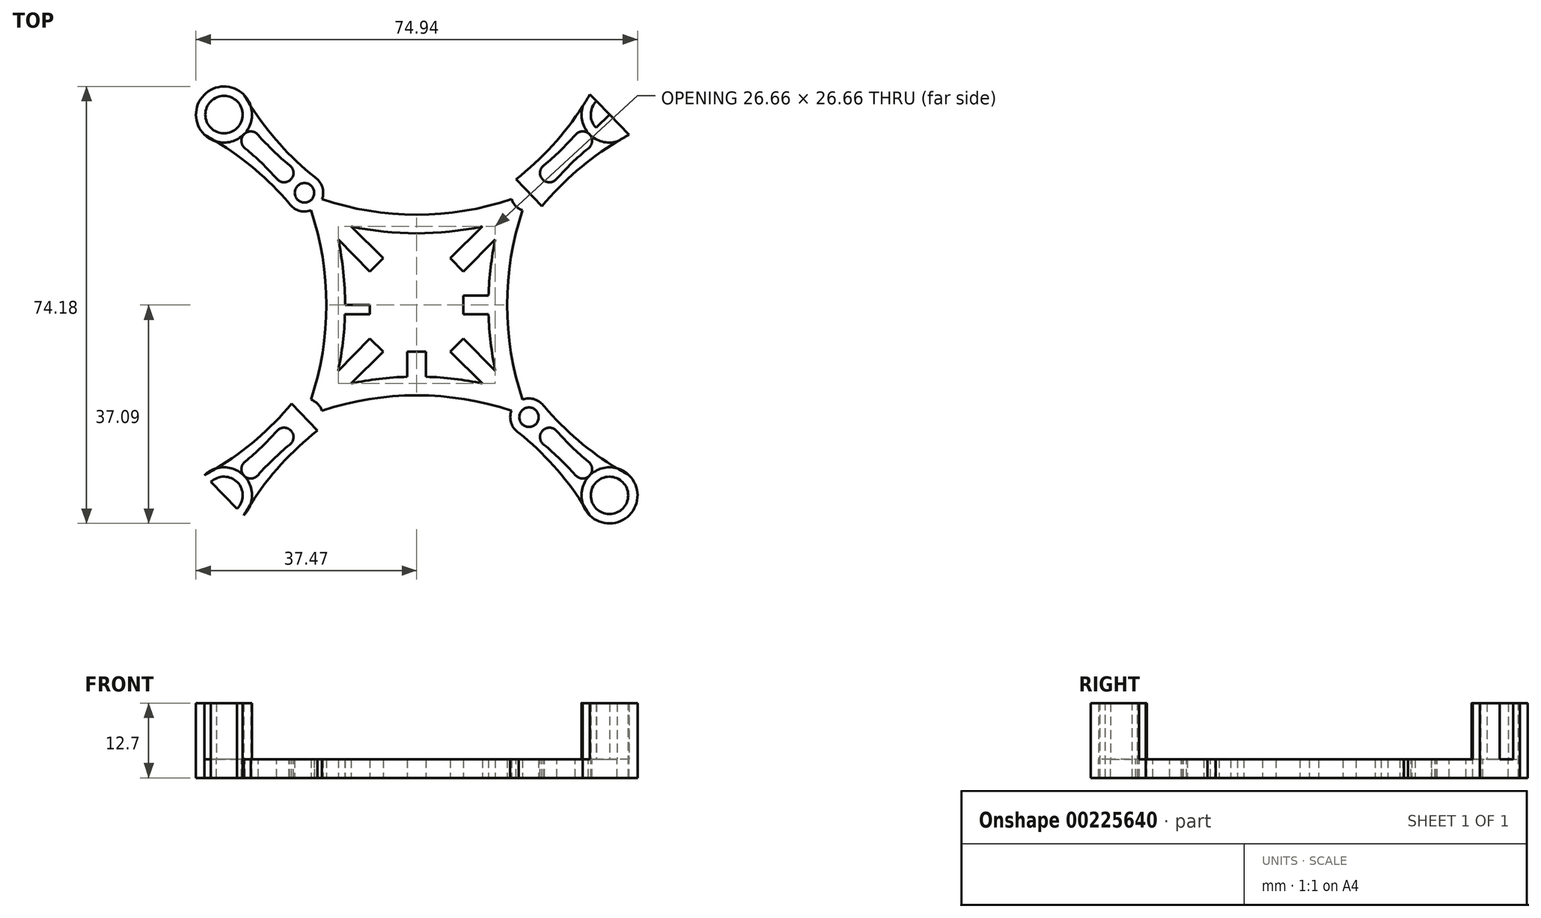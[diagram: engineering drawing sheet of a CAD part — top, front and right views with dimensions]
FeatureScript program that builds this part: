
annotation { "Feature Type Name" : "Feature", "Feature Type Description" : "" }
export const myFeature = defineFeature(function(context is Context, id is Id, definition is map)
    precondition{}
    {
        {
            var Q0;
            Q0=qCreatedBy(makeId("Top.planeOp"),FACE);
            var sketch = newSketch(context, id + "F0", { "sketchPlane" : qUnion([Q0])});
            skPoint(sketch, "E0.middle", {"position": v(0, 0) * mm});
            skLineSegment(sketch, "E1.bottom", {"start": v(-7.94, 7.94) * mm, "end": v(7.94, 7.94) * mm});
            skLineSegment(sketch, "E1.top", {"start": v(-7.94, -7.94) * mm, "end": v(7.94, -7.94) * mm});
            skLineSegment(sketch, "E1.left", {"start": v(-7.94, 7.94) * mm, "end": v(-7.94, -7.94) * mm});
            skLineSegment(sketch, "E1.right", {"start": v(7.94, 7.94) * mm, "end": v(7.94, -7.94) * mm});
            skCircle(sketch, "E2", {"center": v(-19.05, 19.05) * mm, "radius": 3.18 * mm});
            skCircle(sketch, "E3", {"center": v(-19.05, 19.05) * mm, "radius": 1.65 * mm});
            skCircle(sketch, "E4.MirrorC", {"center": v(19.05, 19.05) * mm, "radius": 3.18 * mm});
            skCircle(sketch, "E5.MirrorC", {"center": v(19.05, 19.05) * mm, "radius": 1.65 * mm});
            skCircle(sketch, "E6.MirrorC", {"center": v(-19.05, -19.05) * mm, "radius": 3.18 * mm});
            skCircle(sketch, "E7.MirrorC", {"center": v(-19.05, -19.05) * mm, "radius": 1.65 * mm});
            skCircle(sketch, "E8.MirrorC", {"center": v(19.05, -19.05) * mm, "radius": 3.18 * mm});
            skCircle(sketch, "E9.MirrorC", {"center": v(19.05, -19.05) * mm, "radius": 1.65 * mm});
            skArc(sketch, "E10", {"start": v(-19.05, 19.05) * mm, "mid": v(0, 15.34) * mm, "end": v(19.05, 19.05) * mm});
            skArc(sketch, "E11", {"start": v(19.05, 19.05) * mm, "mid": v(15.34, 0) * mm, "end": v(19.05, -19.05) * mm});
            skArc(sketch, "E12.MirrorCS", {"start": v(19.05, -19.05) * mm, "mid": v(15.34, 0) * mm, "end": v(19.05, 19.05) * mm});
            skArc(sketch, "E13.MirrorCS", {"start": v(19.05, 19.05) * mm, "mid": v(0, 15.34) * mm, "end": v(-19.05, 19.05) * mm});
            skArc(sketch, "E14.MirrorCS", {"start": v(-19.05, -19.05) * mm, "mid": v(-15.34, 0) * mm, "end": v(-19.05, 19.05) * mm});
            skArc(sketch, "E15.MirrorCS", {"start": v(19.05, -19.05) * mm, "mid": v(0, -15.34) * mm, "end": v(-19.05, -19.05) * mm});
            skArc(sketch, "E16.0", {"start": v(14.02, 14.02) * mm, "mid": v(0, 12.17) * mm, "end": v(-14.02, 14.02) * mm});
            skArc(sketch, "E16.1", {"start": v(14.02, 14.02) * mm, "mid": v(12.17, 0) * mm, "end": v(14.02, -14.02) * mm});
            skArc(sketch, "E16.2", {"start": v(14.02, -14.02) * mm, "mid": v(0, -12.17) * mm, "end": v(-14.02, -14.02) * mm});
            skArc(sketch, "E16.3", {"start": v(-14.02, -14.02) * mm, "mid": v(-12.17, 0) * mm, "end": v(-14.02, 14.02) * mm});
            skLineSegment(sketch, "E17.bottom", {"start": v(0, 7.94) * mm, "end": v(-1.59, 7.94) * mm});
            skLineSegment(sketch, "E17.top", {"start": v(0, 13.02) * mm, "end": v(-1.59, 13.02) * mm});
            skLineSegment(sketch, "E17.left", {"start": v(0, 7.94) * mm, "end": v(0, 13.02) * mm});
            skLineSegment(sketch, "E17.right", {"start": v(-1.59, 7.94) * mm, "end": v(-1.59, 13.02) * mm});
            skLineSegment(sketch, "E18.MirrorCS", {"start": v(-1.59, -7.94) * mm, "end": v(-1.59, -13.02) * mm});
            skLineSegment(sketch, "E19.MirrorCS", {"start": v(0, -7.94) * mm, "end": v(0, -13.02) * mm});
            skLineSegment(sketch, "E20.MirrorCS", {"start": v(0, -13.02) * mm, "end": v(-1.59, -13.02) * mm});
            skLineSegment(sketch, "E21.MirrorCS", {"start": v(0, -13.02) * mm, "end": v(1.59, -13.02) * mm});
            skLineSegment(sketch, "E22.MirrorCS", {"start": v(1.59, -7.94) * mm, "end": v(1.59, -13.02) * mm});
            skLineSegment(sketch, "E23.MirrorCS", {"start": v(7.94, -7.94) * mm, "end": v(-7.94, -7.94) * mm});
            skLineSegment(sketch, "E24.MirrorCS", {"start": v(1.59, 7.94) * mm, "end": v(1.59, 13.02) * mm});
            skLineSegment(sketch, "E25.MirrorCS", {"start": v(0, 13.02) * mm, "end": v(1.59, 13.02) * mm});
            skLineSegment(sketch, "E26.bottom", {"start": v(-7.94, 0) * mm, "end": v(-13.02, 0) * mm});
            skLineSegment(sketch, "E26.top", {"start": v(-7.94, 1.59) * mm, "end": v(-13.02, 1.59) * mm});
            skLineSegment(sketch, "E26.left", {"start": v(-7.94, 0) * mm, "end": v(-7.94, 1.59) * mm});
            skLineSegment(sketch, "E26.right", {"start": v(-13.02, 0) * mm, "end": v(-13.02, 1.59) * mm});
            skLineSegment(sketch, "E27.MirrorCS", {"start": v(7.94, 1.59) * mm, "end": v(13.02, 1.59) * mm});
            skLineSegment(sketch, "E28.MirrorCS", {"start": v(13.02, 0) * mm, "end": v(13.02, 1.59) * mm});
            skLineSegment(sketch, "E29.MirrorCS", {"start": v(7.94, 0) * mm, "end": v(13.02, 0) * mm});
            skLineSegment(sketch, "E30.MirrorCS", {"start": v(-13.02, 0) * mm, "end": v(-13.02, -1.59) * mm});
            skLineSegment(sketch, "E31.MirrorCS", {"start": v(-7.94, -1.59) * mm, "end": v(-13.02, -1.59) * mm});
            skLineSegment(sketch, "E32.MirrorCS", {"start": v(7.94, -1.59) * mm, "end": v(13.02, -1.59) * mm});
            skLineSegment(sketch, "E33.MirrorCS", {"start": v(13.02, 0) * mm, "end": v(13.02, -1.59) * mm});
            skLineSegment(sketch, "E34", {"start": v(-7.94, 5.7) * mm, "end": v(-5.7, 7.94) * mm});
            skLineSegment(sketch, "E35", {"start": v(-7.94, 7.94) * mm, "end": v(-6.81, 6.81) * mm});
            skLineSegment(sketch, "E36", {"start": v(-7.94, 5.7) * mm, "end": v(-13.33, 11.15) * mm});
            skLineSegment(sketch, "E37", {"start": v(-13.33, 11.15) * mm, "end": v(-11.13, 13.33) * mm});
            skLineSegment(sketch, "E38", {"start": v(-11.13, 13.33) * mm, "end": v(-5.7, 7.94) * mm});
            skLineSegment(sketch, "E39.MirrorCS", {"start": v(11.13, 13.33) * mm, "end": v(5.7, 7.94) * mm});
            skLineSegment(sketch, "E40.MirrorCS", {"start": v(7.94, 5.7) * mm, "end": v(5.7, 7.94) * mm});
            skLineSegment(sketch, "E41.MirrorCS", {"start": v(7.94, 5.7) * mm, "end": v(13.33, 11.15) * mm});
            skLineSegment(sketch, "E42.MirrorCS", {"start": v(13.33, 11.15) * mm, "end": v(11.13, 13.33) * mm});
            skLineSegment(sketch, "E43.MirrorCS", {"start": v(7.94, -5.7) * mm, "end": v(13.33, -11.15) * mm});
            skLineSegment(sketch, "E44.MirrorCS", {"start": v(7.94, -5.7) * mm, "end": v(5.7, -7.94) * mm});
            skLineSegment(sketch, "E45.MirrorCS", {"start": v(11.13, -13.33) * mm, "end": v(5.7, -7.94) * mm});
            skLineSegment(sketch, "E46.MirrorCS", {"start": v(-7.94, -5.7) * mm, "end": v(-5.7, -7.94) * mm});
            skLineSegment(sketch, "E47.MirrorCS", {"start": v(-11.13, -13.33) * mm, "end": v(-5.7, -7.94) * mm});
            skLineSegment(sketch, "E48.MirrorCS", {"start": v(-13.33, -11.15) * mm, "end": v(-11.13, -13.33) * mm});
            skLineSegment(sketch, "E49.MirrorCS", {"start": v(-7.94, -5.7) * mm, "end": v(-13.33, -11.15) * mm});
            skLineSegment(sketch, "E50.MirrorCS", {"start": v(13.33, -11.15) * mm, "end": v(11.13, -13.33) * mm});
            skLineSegment(sketch, "E51", {"start": v(19.05, -19.05) * mm, "end": v(16.8, -16.81) * mm});
            skPoint(sketch, "E52", {"position": v(17.08, -17.1) * mm});
            skLineSegment(sketch, "E53", {"start": v(17.08, -17.1) * mm, "end": v(17.64, -16.53) * mm});
            skLineSegment(sketch, "E54", {"start": v(17.64, -16.53) * mm, "end": v(16.5, -15.41) * mm});
            skLineSegment(sketch, "E55", {"start": v(16.5, -15.41) * mm, "end": v(15.95, -15.98) * mm});
            skLineSegment(sketch, "E56", {"start": v(15.95, -15.98) * mm, "end": v(16.8, -16.81) * mm});
            skLineSegment(sketch, "E57.MirrorCS", {"start": v(15.4, -16.54) * mm, "end": v(15.95, -15.98) * mm});
            skLineSegment(sketch, "E58.MirrorCS", {"start": v(16.52, -17.66) * mm, "end": v(15.4, -16.54) * mm});
            skLineSegment(sketch, "E59.MirrorCS", {"start": v(17.08, -17.1) * mm, "end": v(16.52, -17.66) * mm});
            skLineSegment(sketch, "E60", {"start": v(15.4, -16.54) * mm, "end": v(14.26, -15.42) * mm});
            skLineSegment(sketch, "E61", {"start": v(14.26, -15.42) * mm, "end": v(15.38, -14.3) * mm});
            skLineSegment(sketch, "E62", {"start": v(15.38, -14.3) * mm, "end": v(16.5, -15.41) * mm});
            skLineSegment(sketch, "E63", {"start": v(15.1, -16.26) * mm, "end": v(16.23, -15.13) * mm});
            skLineSegment(sketch, "E64.MirrorCS", {"start": v(-15.4, -16.54) * mm, "end": v(-14.26, -15.42) * mm});
            skLineSegment(sketch, "E65.MirrorCS", {"start": v(-15.1, -16.26) * mm, "end": v(-16.23, -15.13) * mm});
            skLineSegment(sketch, "E66.MirrorCS", {"start": v(-15.38, -14.3) * mm, "end": v(-16.5, -15.41) * mm});
            skLineSegment(sketch, "E67.MirrorCS", {"start": v(-14.26, -15.42) * mm, "end": v(-15.38, -14.3) * mm});
            skLineSegment(sketch, "E68.MirrorCS", {"start": v(15.38, 14.3) * mm, "end": v(16.5, 15.41) * mm});
            skLineSegment(sketch, "E69.MirrorCS", {"start": v(15.1, 16.26) * mm, "end": v(16.23, 15.13) * mm});
            skLineSegment(sketch, "E70.MirrorCS", {"start": v(15.4, 16.54) * mm, "end": v(14.26, 15.42) * mm});
            skLineSegment(sketch, "E71.MirrorCS", {"start": v(14.26, 15.42) * mm, "end": v(15.38, 14.3) * mm});
            skLineSegment(sketch, "E72.MirrorCS", {"start": v(-15.38, 14.3) * mm, "end": v(-16.5, 15.41) * mm});
            skLineSegment(sketch, "E73.MirrorCS", {"start": v(-15.4, 16.54) * mm, "end": v(-14.26, 15.42) * mm});
            skLineSegment(sketch, "E74.MirrorCS", {"start": v(-14.26, 15.42) * mm, "end": v(-15.38, 14.3) * mm});
            skLineSegment(sketch, "E75.MirrorCS", {"start": v(-15.1, 16.26) * mm, "end": v(-16.23, 15.13) * mm});
            skSolve(sketch);
        }
        {
            var Q0;
            {var subQ0=sQuery(id+"F0.wireOp",EDGE,"E13.MirrorCS");var subQ1=sQuery(id+"F0.wireOp",EDGE,"E2");var subQ2=makeQuery(id+"F0.imprint","INTERSECT",VERTEX,{"derivedFrom":[subQ1,subQ0]});Q0=makeQuery(id+"F0.imprint","IMPRINT",FACE,{"disambiguationData":[TD([[makeQuery(id+"F0.imprint","IMPRINT",EDGE,{"disambiguationData":[TD([[subQ2,-1.0]])],"derivedFrom":subQ1}),1.0]])]});}
            var Q1;
            {var subQ0=sQuery(id+"F0.wireOp",EDGE,"E13.MirrorCS");var subQ1=sQuery(id+"F0.wireOp",EDGE,"E2");var subQ2=makeQuery(id+"F0.imprint","INTERSECT",VERTEX,{"derivedFrom":[subQ1,subQ0]});Q1=makeQuery(id+"F0.imprint","IMPRINT",FACE,{"disambiguationData":[TD([[makeQuery(id+"F0.imprint","IMPRINT",EDGE,{"disambiguationData":[TD([[subQ2,1.0]])],"derivedFrom":subQ1}),1.0]])]});}
            var Q2;
            {var subQ26=sQuery(id+"F0.wireOp",EDGE,"E17.top");Q2=makeQuery(id+"F0.imprint","IMPRINT",FACE,{"disambiguationData":[TD([[makeQuery(id+"F0.imprint","IMPRINT",EDGE,{"derivedFrom":subQ26}),-1.0]])]});}
            var Q3;
            {var subQ0=sQuery(id+"F0.wireOp",EDGE,"E11");var subQ1=sQuery(id+"F0.wireOp",EDGE,"E4.MirrorC");var subQ2=makeQuery(id+"F0.imprint","INTERSECT",VERTEX,{"derivedFrom":[subQ1,subQ0]});Q3=makeQuery(id+"F0.imprint","IMPRINT",FACE,{"disambiguationData":[TD([[makeQuery(id+"F0.imprint","IMPRINT",EDGE,{"disambiguationData":[TD([[subQ2,-1.0]])],"derivedFrom":subQ1}),-1.0]])]});}
            var Q4;
            {var subQ0=sQuery(id+"F0.wireOp",EDGE,"E11");var subQ1=sQuery(id+"F0.wireOp",EDGE,"E4.MirrorC");var subQ2=makeQuery(id+"F0.imprint","INTERSECT",VERTEX,{"derivedFrom":[subQ1,subQ0]});Q4=makeQuery(id+"F0.imprint","IMPRINT",FACE,{"disambiguationData":[TD([[makeQuery(id+"F0.imprint","IMPRINT",EDGE,{"disambiguationData":[TD([[subQ2,1.0]])],"derivedFrom":subQ1}),-1.0]])]});}
            var Q5;
            {var subQ5=sQuery(id+"F0.wireOp",EDGE,"E17.top");Q5=makeQuery(id+"F0.imprint","IMPRINT",FACE,{"disambiguationData":[TD([[makeQuery(id+"F0.imprint","IMPRINT",EDGE,{"derivedFrom":subQ5}),1.0]])]});}
            var Q6;
            {var subQ3=sQuery(id+"F0.wireOp",EDGE,"E37");Q6=makeQuery(id+"F0.imprint","IMPRINT",FACE,{"disambiguationData":[TD([[makeQuery(id+"F0.imprint","IMPRINT",EDGE,{"derivedFrom":subQ3}),1.0]])]});}
            var Q7;
            {var subQ5=sQuery(id+"F0.wireOp",EDGE,"E25.MirrorCS");Q7=makeQuery(id+"F0.imprint","IMPRINT",FACE,{"disambiguationData":[TD([[makeQuery(id+"F0.imprint","IMPRINT",EDGE,{"derivedFrom":subQ5}),-1.0]])]});}
            var Q8;
            {var subQ3=sQuery(id+"F0.wireOp",EDGE,"E42.MirrorCS");Q8=makeQuery(id+"F0.imprint","IMPRINT",FACE,{"disambiguationData":[TD([[makeQuery(id+"F0.imprint","IMPRINT",EDGE,{"derivedFrom":subQ3}),-1.0]])]});}
            var Q9;
            {var subQ1=sQuery(id+"F0.wireOp",EDGE,"E39.MirrorCS");Q9=makeQuery(id+"F0.imprint","IMPRINT",FACE,{"disambiguationData":[TD([[makeQuery(id+"F0.imprint","IMPRINT",EDGE,{"derivedFrom":subQ1}),1.0]])]});}
            var Q10;
            {var subQ5=sQuery(id+"F0.wireOp",EDGE,"E36");Q10=makeQuery(id+"F0.imprint","IMPRINT",FACE,{"disambiguationData":[TD([[makeQuery(id+"F0.imprint","IMPRINT",EDGE,{"derivedFrom":subQ5}),-1.0]])]});}
            var Q11;
            {var subQ5=sQuery(id+"F0.wireOp",EDGE,"E17.bottom");Q11=makeQuery(id+"F0.imprint","IMPRINT",FACE,{"disambiguationData":[TD([[makeQuery(id+"F0.imprint","IMPRINT",EDGE,{"derivedFrom":subQ5}),-1.0]])]});}
            var Q12;
            {var subQ3=sQuery(id+"F0.wireOp",EDGE,"E24.MirrorCS");var subQ5=sQuery(id+"F0.wireOp",EDGE,"E16.0");var subQ6=makeQuery(id+"F0.imprint","INTERSECT",VERTEX,{"derivedFrom":[subQ5,subQ3]});Q12=makeQuery(id+"F0.imprint","IMPRINT",FACE,{"disambiguationData":[TD([[makeQuery(id+"F0.imprint","IMPRINT",EDGE,{"disambiguationData":[TD([[subQ6,-1.0]])],"derivedFrom":subQ5}),1.0]])]});}
            var Q13;
            {var subQ0=sQuery(id+"F0.wireOp",EDGE,"E35");Q13=makeQuery(id+"F0.imprint","IMPRINT",FACE,{"disambiguationData":[TD([[makeQuery(id+"F0.imprint","IMPRINT",EDGE,{"derivedFrom":subQ0}),1.0]])]});}
            var Q14;
            {var subQ0=sQuery(id+"F0.wireOp",EDGE,"E35");Q14=makeQuery(id+"F0.imprint","IMPRINT",FACE,{"disambiguationData":[TD([[makeQuery(id+"F0.imprint","IMPRINT",EDGE,{"derivedFrom":subQ0}),-1.0]])]});}
            var Q15;
            {var subQ3=sQuery(id+"F0.wireOp",EDGE,"E40.MirrorCS");Q15=makeQuery(id+"F0.imprint","IMPRINT",FACE,{"disambiguationData":[TD([[makeQuery(id+"F0.imprint","IMPRINT",EDGE,{"derivedFrom":subQ3}),-1.0]])]});}
            var Q16;
            {var subQ12=sQuery(id+"F0.wireOp",EDGE,"E17.bottom");Q16=makeQuery(id+"F0.imprint","IMPRINT",FACE,{"disambiguationData":[TD([[makeQuery(id+"F0.imprint","IMPRINT",EDGE,{"derivedFrom":subQ12}),1.0]])]});}
            var Q17;
            {var subQ5=sQuery(id+"F0.wireOp",EDGE,"E26.right");Q17=makeQuery(id+"F0.imprint","IMPRINT",FACE,{"disambiguationData":[TD([[makeQuery(id+"F0.imprint","IMPRINT",EDGE,{"derivedFrom":subQ5}),-1.0]])]});}
            var Q18;
            {var subQ5=sQuery(id+"F0.wireOp",EDGE,"E30.MirrorCS");Q18=makeQuery(id+"F0.imprint","IMPRINT",FACE,{"disambiguationData":[TD([[makeQuery(id+"F0.imprint","IMPRINT",EDGE,{"derivedFrom":subQ5}),1.0]])]});}
            var Q19;
            {var subQ3=sQuery(id+"F0.wireOp",EDGE,"E31.MirrorCS");var subQ5=sQuery(id+"F0.wireOp",EDGE,"E16.3");var subQ6=makeQuery(id+"F0.imprint","INTERSECT",VERTEX,{"derivedFrom":[subQ5,subQ3]});Q19=makeQuery(id+"F0.imprint","IMPRINT",FACE,{"disambiguationData":[TD([[makeQuery(id+"F0.imprint","IMPRINT",EDGE,{"disambiguationData":[TD([[subQ6,-1.0]])],"derivedFrom":subQ5}),-1.0]])]});}
            var Q20;
            {var subQ5=sQuery(id+"F0.wireOp",EDGE,"E26.left");Q20=makeQuery(id+"F0.imprint","IMPRINT",FACE,{"disambiguationData":[TD([[makeQuery(id+"F0.imprint","IMPRINT",EDGE,{"derivedFrom":subQ5}),1.0]])]});}
            var Q21;
            {var subQ5=sQuery(id+"F0.wireOp",EDGE,"E28.MirrorCS");Q21=makeQuery(id+"F0.imprint","IMPRINT",FACE,{"disambiguationData":[TD([[makeQuery(id+"F0.imprint","IMPRINT",EDGE,{"derivedFrom":subQ5}),1.0]])]});}
            var Q22;
            {var subQ5=sQuery(id+"F0.wireOp",EDGE,"E33.MirrorCS");Q22=makeQuery(id+"F0.imprint","IMPRINT",FACE,{"disambiguationData":[TD([[makeQuery(id+"F0.imprint","IMPRINT",EDGE,{"derivedFrom":subQ5}),-1.0]])]});}
            var Q23;
            {var subQ3=sQuery(id+"F0.wireOp",EDGE,"E46.MirrorCS");Q23=makeQuery(id+"F0.imprint","IMPRINT",FACE,{"disambiguationData":[TD([[makeQuery(id+"F0.imprint","IMPRINT",EDGE,{"derivedFrom":subQ3}),-1.0]])]});}
            var Q24;
            {var subQ3=sQuery(id+"F0.wireOp",EDGE,"E48.MirrorCS");Q24=makeQuery(id+"F0.imprint","IMPRINT",FACE,{"disambiguationData":[TD([[makeQuery(id+"F0.imprint","IMPRINT",EDGE,{"derivedFrom":subQ3}),-1.0]])]});}
            var Q25;
            {var subQ0=sQuery(id+"F0.wireOp",EDGE,"E14.MirrorCS");var subQ1=sQuery(id+"F0.wireOp",EDGE,"E6.MirrorC");var subQ2=makeQuery(id+"F0.imprint","INTERSECT",VERTEX,{"derivedFrom":[subQ1,subQ0]});Q25=makeQuery(id+"F0.imprint","IMPRINT",FACE,{"disambiguationData":[TD([[makeQuery(id+"F0.imprint","IMPRINT",EDGE,{"disambiguationData":[TD([[subQ2,-1.0]])],"derivedFrom":subQ1}),-1.0]])]});}
            var Q26;
            {var subQ0=sQuery(id+"F0.wireOp",EDGE,"E14.MirrorCS");var subQ1=sQuery(id+"F0.wireOp",EDGE,"E6.MirrorC");var subQ2=makeQuery(id+"F0.imprint","INTERSECT",VERTEX,{"derivedFrom":[subQ1,subQ0]});Q26=makeQuery(id+"F0.imprint","IMPRINT",FACE,{"disambiguationData":[TD([[makeQuery(id+"F0.imprint","IMPRINT",EDGE,{"disambiguationData":[TD([[subQ2,1.0]])],"derivedFrom":subQ1}),-1.0]])]});}
            var Q27;
            {var subQ5=sQuery(id+"F0.wireOp",EDGE,"E20.MirrorCS");Q27=makeQuery(id+"F0.imprint","IMPRINT",FACE,{"disambiguationData":[TD([[makeQuery(id+"F0.imprint","IMPRINT",EDGE,{"derivedFrom":subQ5}),-1.0]])]});}
            var Q28;
            {var subQ5=sQuery(id+"F0.wireOp",EDGE,"E21.MirrorCS");Q28=makeQuery(id+"F0.imprint","IMPRINT",FACE,{"disambiguationData":[TD([[makeQuery(id+"F0.imprint","IMPRINT",EDGE,{"derivedFrom":subQ5}),1.0]])]});}
            var Q29;
            {var subQ0=sQuery(id+"F0.wireOp",EDGE,"E11");var subQ1=sQuery(id+"F0.wireOp",EDGE,"E8.MirrorC");var subQ2=makeQuery(id+"F0.imprint","INTERSECT",VERTEX,{"derivedFrom":[subQ1,subQ0]});Q29=makeQuery(id+"F0.imprint","IMPRINT",FACE,{"disambiguationData":[TD([[makeQuery(id+"F0.imprint","IMPRINT",EDGE,{"disambiguationData":[TD([[subQ2,1.0]])],"derivedFrom":subQ1}),1.0]])]});}
            var Q30;
            {var subQ0=sQuery(id+"F0.wireOp",EDGE,"E11");var subQ1=sQuery(id+"F0.wireOp",EDGE,"E8.MirrorC");var subQ2=makeQuery(id+"F0.imprint","INTERSECT",VERTEX,{"derivedFrom":[subQ1,subQ0]});Q30=makeQuery(id+"F0.imprint","IMPRINT",FACE,{"disambiguationData":[TD([[makeQuery(id+"F0.imprint","IMPRINT",EDGE,{"disambiguationData":[TD([[subQ2,-1.0]])],"derivedFrom":subQ1}),1.0]])]});}
            var Q31;
            {var subQ0=sQuery(id+"F0.wireOp",EDGE,"E29.MirrorCS");var subQ1=sQuery(id+"F0.wireOp",EDGE,"E1.right");var subQ2=makeQuery(id+"F0.imprint","INTERSECT",VERTEX,{"derivedFrom":[subQ1,subQ0]});Q31=makeQuery(id+"F0.imprint","IMPRINT",FACE,{"disambiguationData":[TD([[makeQuery(id+"F0.imprint","IMPRINT",EDGE,{"disambiguationData":[TD([[subQ2,-1.0]])],"derivedFrom":subQ1}),1.0]])]});}
            var Q32;
            {var subQ0=sQuery(id+"F0.wireOp",EDGE,"E27.MirrorCS");var subQ1=sQuery(id+"F0.wireOp",EDGE,"E1.right");var subQ2=makeQuery(id+"F0.imprint","INTERSECT",VERTEX,{"derivedFrom":[subQ1,subQ0]});Q32=makeQuery(id+"F0.imprint","IMPRINT",FACE,{"disambiguationData":[TD([[makeQuery(id+"F0.imprint","IMPRINT",EDGE,{"disambiguationData":[TD([[subQ2,-1.0]])],"derivedFrom":subQ1}),1.0]])]});}
            var Q33;
            {var subQ0=sQuery(id+"F0.wireOp",EDGE,"E47.MirrorCS");Q33=makeQuery(id+"F0.imprint","IMPRINT",FACE,{"disambiguationData":[TD([[makeQuery(id+"F0.imprint","IMPRINT",EDGE,{"derivedFrom":subQ0}),1.0]])]});}
            var Q34;
            {var subQ3=sQuery(id+"F0.wireOp",EDGE,"E44.MirrorCS");Q34=makeQuery(id+"F0.imprint","IMPRINT",FACE,{"disambiguationData":[TD([[makeQuery(id+"F0.imprint","IMPRINT",EDGE,{"derivedFrom":subQ3}),1.0]])]});}
            var Q35;
            {var subQ3=sQuery(id+"F0.wireOp",EDGE,"E50.MirrorCS");Q35=makeQuery(id+"F0.imprint","IMPRINT",FACE,{"disambiguationData":[TD([[makeQuery(id+"F0.imprint","IMPRINT",EDGE,{"derivedFrom":subQ3}),1.0]])]});}
            var Q36;
            {var subQ1=sQuery(id+"F0.wireOp",EDGE,"E43.MirrorCS");Q36=makeQuery(id+"F0.imprint","IMPRINT",FACE,{"disambiguationData":[TD([[makeQuery(id+"F0.imprint","IMPRINT",EDGE,{"derivedFrom":subQ1}),-1.0]])]});}
            var Q37;
            {var subQ0=sQuery(id+"F0.wireOp",EDGE,"E22.MirrorCS");var subQ1=sQuery(id+"F0.wireOp",EDGE,"E16.2");var subQ2=makeQuery(id+"F0.imprint","INTERSECT",VERTEX,{"derivedFrom":[subQ1,subQ0]});Q37=makeQuery(id+"F0.imprint","IMPRINT",FACE,{"disambiguationData":[TD([[makeQuery(id+"F0.imprint","IMPRINT",EDGE,{"disambiguationData":[TD([[subQ2,-1.0]])],"derivedFrom":subQ1}),-1.0]])]});}
            var Q38;
            {var subQ0=sQuery(id+"F0.wireOp",EDGE,"E19.MirrorCS");var subQ1=sQuery(id+"F0.wireOp",EDGE,"E16.2");var subQ2=makeQuery(id+"F0.imprint","INTERSECT",VERTEX,{"derivedFrom":[subQ1,subQ0]});Q38=makeQuery(id+"F0.imprint","IMPRINT",FACE,{"disambiguationData":[TD([[makeQuery(id+"F0.imprint","IMPRINT",EDGE,{"disambiguationData":[TD([[subQ2,-1.0]])],"derivedFrom":subQ1}),-1.0]])]});}
            var Q39;
            {var subQ5=sQuery(id+"F0.wireOp",EDGE,"E59.MirrorCS");Q39=makeQuery(id+"F0.imprint","IMPRINT",FACE,{"disambiguationData":[TD([[makeQuery(id+"F0.imprint","IMPRINT",EDGE,{"derivedFrom":subQ5}),1.0]])]});}
            var Q40;
            {var subQ0=sQuery(id+"F0.wireOp",EDGE,"E56");Q40=makeQuery(id+"F0.imprint","IMPRINT",FACE,{"disambiguationData":[TD([[makeQuery(id+"F0.imprint","IMPRINT",EDGE,{"derivedFrom":subQ0}),-1.0]])]});}
            var Q41;
            {var subQ5=sQuery(id+"F0.wireOp",EDGE,"E59.MirrorCS");Q41=makeQuery(id+"F0.imprint","IMPRINT",FACE,{"disambiguationData":[TD([[makeQuery(id+"F0.imprint","IMPRINT",EDGE,{"derivedFrom":subQ5}),-1.0]])]});}
            var Q42;
            {var subQ5=sQuery(id+"F0.wireOp",EDGE,"E53");Q42=makeQuery(id+"F0.imprint","IMPRINT",FACE,{"disambiguationData":[TD([[makeQuery(id+"F0.imprint","IMPRINT",EDGE,{"derivedFrom":subQ5}),1.0]])]});}
            var Q43;
            {var subQ4=sQuery(id+"F0.wireOp",EDGE,"E55");Q43=makeQuery(id+"F0.imprint","IMPRINT",FACE,{"disambiguationData":[TD([[makeQuery(id+"F0.imprint","IMPRINT",EDGE,{"derivedFrom":subQ4}),1.0]])]});}
            var Q44;
            {var subQ1=sQuery(id+"F0.wireOp",EDGE,"E55");Q44=makeQuery(id+"F0.imprint","IMPRINT",FACE,{"disambiguationData":[TD([[makeQuery(id+"F0.imprint","IMPRINT",EDGE,{"derivedFrom":subQ1}),-1.0]])]});}
            var Q45;
            {var subQ2=sQuery(id+"F0.wireOp",EDGE,"E69.MirrorCS");Q45=makeQuery(id+"F0.imprint","IMPRINT",FACE,{"disambiguationData":[TD([[makeQuery(id+"F0.imprint","IMPRINT",EDGE,{"derivedFrom":subQ2}),-1.0]])]});}
            var Q46;
            {var subQ0=sQuery(id+"F0.wireOp",EDGE,"E61");Q46=makeQuery(id+"F0.imprint","IMPRINT",FACE,{"disambiguationData":[TD([[makeQuery(id+"F0.imprint","IMPRINT",EDGE,{"derivedFrom":subQ0}),-1.0]])]});}
            var Q47;
            {var subQ2=sQuery(id+"F0.wireOp",EDGE,"E65.MirrorCS");Q47=makeQuery(id+"F0.imprint","IMPRINT",FACE,{"disambiguationData":[TD([[makeQuery(id+"F0.imprint","IMPRINT",EDGE,{"derivedFrom":subQ2}),-1.0]])]});}
            var Q48;
            {var subQ0=sQuery(id+"F0.wireOp",EDGE,"E74.MirrorCS");Q48=makeQuery(id+"F0.imprint","IMPRINT",FACE,{"disambiguationData":[TD([[makeQuery(id+"F0.imprint","IMPRINT",EDGE,{"derivedFrom":subQ0}),-1.0]])]});}
            extrude(context, id + "F1", {"entities" : qUnion([Q0, Q1, Q2, Q3, Q4, Q5, Q6, Q7, Q8, Q9, Q10, Q11, Q12, Q13, Q14, Q15, Q16, Q17, Q18, Q19, Q20, Q21, Q22, Q23, Q24, Q25, Q26, Q27, Q28, Q29, Q30, Q31, Q32, Q33, Q34, Q35, Q36, Q37, Q38, Q39, Q40, Q41, Q42, Q43, Q44, Q45, Q46, Q47, Q48]), "depth" : 3.17 * mm});
        }
        {
            var Q0;
            Q0=makeQuery(id+"F1.opExtrude","CAP_FACE",FACE,{"disambiguationData":[OSD([sQuery(id+"F0.wireOp",EDGE,"E1.bottom"),sQuery(id+"F0.wireOp",EDGE,"E1.left"),sQuery(id+"F0.wireOp",EDGE,"E1.right"),sQuery(id+"F0.wireOp",EDGE,"E2"),sQuery(id+"F0.wireOp",EDGE,"E3"),sQuery(id+"F0.wireOp",EDGE,"E4.MirrorC"),sQuery(id+"F0.wireOp",EDGE,"E5.MirrorC"),sQuery(id+"F0.wireOp",EDGE,"E6.MirrorC"),sQuery(id+"F0.wireOp",EDGE,"E7.MirrorC"),sQuery(id+"F0.wireOp",EDGE,"E8.MirrorC"),sQuery(id+"F0.wireOp",EDGE,"E9.MirrorC"),sQuery(id+"F0.wireOp",EDGE,"E11"),sQuery(id+"F0.wireOp",EDGE,"E13.MirrorCS"),sQuery(id+"F0.wireOp",EDGE,"E14.MirrorCS"),sQuery(id+"F0.wireOp",EDGE,"E15.MirrorCS"),sQuery(id+"F0.wireOp",EDGE,"E16.0"),sQuery(id+"F0.wireOp",EDGE,"E16.1"),sQuery(id+"F0.wireOp",EDGE,"E16.2"),sQuery(id+"F0.wireOp",EDGE,"E16.3"),sQuery(id+"F0.wireOp",EDGE,"E17.right"),sQuery(id+"F0.wireOp",EDGE,"E18.MirrorCS"),sQuery(id+"F0.wireOp",EDGE,"E22.MirrorCS"),sQuery(id+"F0.wireOp",EDGE,"E23.MirrorCS"),sQuery(id+"F0.wireOp",EDGE,"E24.MirrorCS"),sQuery(id+"F0.wireOp",EDGE,"E26.top"),sQuery(id+"F0.wireOp",EDGE,"E27.MirrorCS"),sQuery(id+"F0.wireOp",EDGE,"E31.MirrorCS"),sQuery(id+"F0.wireOp",EDGE,"E32.MirrorCS"),sQuery(id+"F0.wireOp",EDGE,"E36"),sQuery(id+"F0.wireOp",EDGE,"E38"),sQuery(id+"F0.wireOp",EDGE,"E39.MirrorCS"),sQuery(id+"F0.wireOp",EDGE,"E41.MirrorCS"),sQuery(id+"F0.wireOp",EDGE,"E43.MirrorCS"),sQuery(id+"F0.wireOp",EDGE,"E45.MirrorCS"),sQuery(id+"F0.wireOp",EDGE,"E47.MirrorCS"),sQuery(id+"F0.wireOp",EDGE,"E49.MirrorCS")])],"isStart":false});
            var sketch = newSketch(context, id + "F2", { "sketchPlane" : qUnion([Q0])});
            skPoint(sketch, "E76", {"position": v(19.05, -19.05) * mm});
            skLineSegment(sketch, "E77", {"start": v(19.05, -19.05) * mm, "end": v(32.7, -32.33) * mm});
            skLineSegment(sketch, "E78", {"start": v(19.05, -19.05) * mm, "end": v(19.05, -15.88) * mm});
            skCircle(sketch, "E79", {"center": v(32.7, -32.33) * mm, "radius": 4.76 * mm});
            skCircle(sketch, "E80", {"center": v(32.7, -32.33) * mm, "radius": 3.18 * mm});
            skLineSegment(sketch, "E81", {"start": v(32.7, -32.33) * mm, "end": v(29.39, -35.74) * mm});
            skLineSegment(sketch, "E82", {"start": v(32.7, -32.33) * mm, "end": v(36.03, -28.92) * mm});
            skLineSegment(sketch, "E83", {"start": v(19.05, -19.05) * mm, "end": v(21.26, -16.77) * mm});
            skLineSegment(sketch, "E84", {"start": v(19.05, -19.05) * mm, "end": v(16.84, -21.33) * mm});
            skArc(sketch, "E85", {"start": v(29.39, -35.74) * mm, "mid": v(23.8, -27.94) * mm, "end": v(16.84, -21.33) * mm});
            skArc(sketch, "E86", {"start": v(21.26, -16.77) * mm, "mid": v(28.07, -23.55) * mm, "end": v(36.03, -28.92) * mm});
            skLineSegment(sketch, "E87.MirrorCS", {"start": v(-19.05, -19.05) * mm, "end": v(-16.84, -21.33) * mm});
            skLineSegment(sketch, "E88.MirrorCS", {"start": v(-19.05, -19.05) * mm, "end": v(-21.26, -16.77) * mm});
            skLineSegment(sketch, "E89.MirrorCS", {"start": v(-19.05, -19.05) * mm, "end": v(-19.05, -15.88) * mm});
            skCircle(sketch, "E90.MirrorC", {"center": v(-32.7, -32.33) * mm, "radius": 3.18 * mm});
            skLineSegment(sketch, "E91.MirrorCS", {"start": v(-32.7, -32.33) * mm, "end": v(-29.39, -35.74) * mm});
            skLineSegment(sketch, "E92.MirrorCS", {"start": v(-32.7, -32.33) * mm, "end": v(-36.03, -28.92) * mm});
            skArc(sketch, "E93.MirrorCS", {"start": v(-21.26, -16.77) * mm, "mid": v(-28.07, -23.55) * mm, "end": v(-36.03, -28.92) * mm});
            skArc(sketch, "E94.MirrorCS", {"start": v(-29.39, -35.74) * mm, "mid": v(-23.8, -27.94) * mm, "end": v(-16.84, -21.33) * mm});
            skPoint(sketch, "E95.MirrorP", {"position": v(-19.05, -19.05) * mm});
            skLineSegment(sketch, "E96.MirrorCS", {"start": v(-19.05, -19.05) * mm, "end": v(-32.7, -32.33) * mm});
            skCircle(sketch, "E97.MirrorC", {"center": v(-32.7, -32.33) * mm, "radius": 4.76 * mm});
            skLineSegment(sketch, "E98.MirrorCS", {"start": v(-19.05, 19.05) * mm, "end": v(-16.84, 21.33) * mm});
            skLineSegment(sketch, "E99.MirrorCS", {"start": v(-32.7, 32.33) * mm, "end": v(-29.39, 35.74) * mm});
            skLineSegment(sketch, "E100.MirrorCS", {"start": v(19.05, 19.05) * mm, "end": v(21.26, 16.77) * mm});
            skLineSegment(sketch, "E101.MirrorCS", {"start": v(19.05, 19.05) * mm, "end": v(16.84, 21.33) * mm});
            skLineSegment(sketch, "E102.MirrorCS", {"start": v(-19.05, 19.05) * mm, "end": v(-21.26, 16.77) * mm});
            skLineSegment(sketch, "E103.MirrorCS", {"start": v(32.7, 32.33) * mm, "end": v(36.03, 28.92) * mm});
            skLineSegment(sketch, "E104.MirrorCS", {"start": v(32.7, 32.33) * mm, "end": v(29.39, 35.74) * mm});
            skLineSegment(sketch, "E105.MirrorCS", {"start": v(19.05, 19.05) * mm, "end": v(19.05, 15.88) * mm});
            skLineSegment(sketch, "E106.MirrorCS", {"start": v(-32.7, 32.33) * mm, "end": v(-36.03, 28.92) * mm});
            skLineSegment(sketch, "E107.MirrorCS", {"start": v(-19.05, 19.05) * mm, "end": v(-19.05, 15.88) * mm});
            skLineSegment(sketch, "E108.MirrorCS", {"start": v(19.05, 19.05) * mm, "end": v(32.7, 32.33) * mm});
            skPoint(sketch, "E109.MirrorP", {"position": v(-19.05, 19.05) * mm});
            skArc(sketch, "E110.MirrorCS", {"start": v(-29.39, 35.74) * mm, "mid": v(-23.8, 27.94) * mm, "end": v(-16.84, 21.33) * mm});
            skPoint(sketch, "E111.MirrorP", {"position": v(19.05, 19.05) * mm});
            skLineSegment(sketch, "E112.MirrorCS", {"start": v(-19.05, 19.05) * mm, "end": v(-32.7, 32.33) * mm});
            skCircle(sketch, "E113.MirrorC", {"center": v(-32.7, 32.33) * mm, "radius": 4.76 * mm});
            skCircle(sketch, "E114.MirrorC", {"center": v(32.7, 32.33) * mm, "radius": 3.18 * mm});
            skCircle(sketch, "E115.MirrorC", {"center": v(32.7, 32.33) * mm, "radius": 4.76 * mm});
            skCircle(sketch, "E116.MirrorC", {"center": v(-32.7, 32.33) * mm, "radius": 3.18 * mm});
            skArc(sketch, "E117.MirrorCS", {"start": v(-21.26, 16.77) * mm, "mid": v(-28.07, 23.55) * mm, "end": v(-36.03, 28.92) * mm});
            skArc(sketch, "E118.MirrorCS", {"start": v(29.39, 35.74) * mm, "mid": v(23.8, 27.94) * mm, "end": v(16.84, 21.33) * mm});
            skArc(sketch, "E119.MirrorCS", {"start": v(21.26, 16.77) * mm, "mid": v(28.07, 23.55) * mm, "end": v(36.03, 28.92) * mm});
            skSolve(sketch);
        }
        {
            var Q0;
            {var subQ0=sQuery(id+"F2.wireOp",EDGE,"E86");var subQ1=sQuery(id+"F2.wireOp",EDGE,"E79");var subQ3=makeQuery(id+"F2.imprint","INTERSECT",VERTEX,{"derivedFrom":[subQ1,subQ0]});Q0=makeQuery(id+"F2.imprint","IMPRINT",FACE,{"disambiguationData":[TD([[makeQuery(id+"F2.imprint","IMPRINT",EDGE,{"disambiguationData":[TD([[subQ3,1.0]])],"derivedFrom":subQ1}),1.0]])]});}
            var Q1;
            {var subQ0=sQuery(id+"F2.wireOp",EDGE,"E85");var subQ1=sQuery(id+"F2.wireOp",EDGE,"E79");var subQ3=makeQuery(id+"F2.imprint","INTERSECT",VERTEX,{"derivedFrom":[subQ1,subQ0]});Q1=makeQuery(id+"F2.imprint","IMPRINT",FACE,{"disambiguationData":[TD([[makeQuery(id+"F2.imprint","IMPRINT",EDGE,{"disambiguationData":[TD([[subQ3,-1.0]])],"derivedFrom":subQ1}),1.0]])]});}
            var Q2;
            {var subQ0=sQuery(id+"F2.wireOp",EDGE,"E97.MirrorC");var subQ1=sQuery(id+"F2.wireOp",EDGE,"E93.MirrorCS");var subQ3=makeQuery(id+"F2.imprint","INTERSECT",VERTEX,{"derivedFrom":[subQ1,subQ0]});Q2=makeQuery(id+"F2.imprint","IMPRINT",FACE,{"disambiguationData":[TD([[makeQuery(id+"F2.imprint","IMPRINT",EDGE,{"disambiguationData":[TD([[subQ3,-1.0]])],"derivedFrom":subQ1}),-1.0]])]});}
            var Q3;
            {var subQ0=sQuery(id+"F2.wireOp",EDGE,"E97.MirrorC");var subQ1=sQuery(id+"F2.wireOp",EDGE,"E94.MirrorCS");var subQ3=makeQuery(id+"F2.imprint","INTERSECT",VERTEX,{"derivedFrom":[subQ1,subQ0]});Q3=makeQuery(id+"F2.imprint","IMPRINT",FACE,{"disambiguationData":[TD([[makeQuery(id+"F2.imprint","IMPRINT",EDGE,{"disambiguationData":[TD([[subQ3,1.0]])],"derivedFrom":subQ1}),-1.0]])]});}
            var Q4;
            {var subQ0=sQuery(id+"F2.wireOp",EDGE,"E113.MirrorC");var subQ1=sQuery(id+"F2.wireOp",EDGE,"E110.MirrorCS");var subQ3=makeQuery(id+"F2.imprint","INTERSECT",VERTEX,{"derivedFrom":[subQ1,subQ0]});Q4=makeQuery(id+"F2.imprint","IMPRINT",FACE,{"disambiguationData":[TD([[makeQuery(id+"F2.imprint","IMPRINT",EDGE,{"disambiguationData":[TD([[subQ3,1.0]])],"derivedFrom":subQ1}),1.0]])]});}
            var Q5;
            {var subQ0=sQuery(id+"F2.wireOp",EDGE,"E117.MirrorCS");var subQ1=sQuery(id+"F2.wireOp",EDGE,"E113.MirrorC");var subQ3=makeQuery(id+"F2.imprint","INTERSECT",VERTEX,{"derivedFrom":[subQ1,subQ0]});Q5=makeQuery(id+"F2.imprint","IMPRINT",FACE,{"disambiguationData":[TD([[makeQuery(id+"F2.imprint","IMPRINT",EDGE,{"disambiguationData":[TD([[subQ3,1.0]])],"derivedFrom":subQ1}),1.0]])]});}
            var Q6;
            {var subQ0=sQuery(id+"F2.wireOp",EDGE,"E119.MirrorCS");var subQ1=sQuery(id+"F2.wireOp",EDGE,"E115.MirrorC");var subQ3=makeQuery(id+"F2.imprint","INTERSECT",VERTEX,{"derivedFrom":[subQ1,subQ0]});Q6=makeQuery(id+"F2.imprint","IMPRINT",FACE,{"disambiguationData":[TD([[makeQuery(id+"F2.imprint","IMPRINT",EDGE,{"disambiguationData":[TD([[subQ3,1.0]])],"derivedFrom":subQ1}),-1.0]])]});}
            var Q7;
            {var subQ0=sQuery(id+"F2.wireOp",EDGE,"E118.MirrorCS");var subQ1=sQuery(id+"F2.wireOp",EDGE,"E115.MirrorC");var subQ3=makeQuery(id+"F2.imprint","INTERSECT",VERTEX,{"derivedFrom":[subQ1,subQ0]});Q7=makeQuery(id+"F2.imprint","IMPRINT",FACE,{"disambiguationData":[TD([[makeQuery(id+"F2.imprint","IMPRINT",EDGE,{"disambiguationData":[TD([[subQ3,-1.0]])],"derivedFrom":subQ1}),-1.0]])]});}
            var Q8;
            {var subQ3=sQuery(id+"F2.wireOp",EDGE,"E82");var subQ5=sQuery(id+"F2.wireOp",EDGE,"E80");var subQ7=makeQuery(id+"F2.imprint","INTERSECT",VERTEX,{"derivedFrom":[subQ5,subQ3]});Q8=makeQuery(id+"F2.imprint","IMPRINT",FACE,{"disambiguationData":[TD([[makeQuery(id+"F2.imprint","IMPRINT",EDGE,{"disambiguationData":[TD([[subQ7,1.0]])],"derivedFrom":subQ5}),-1.0]])]});}
            var Q9;
            {var subQ0=sQuery(id+"F2.wireOp",EDGE,"E92.MirrorCS");var subQ1=sQuery(id+"F2.wireOp",EDGE,"E90.MirrorC");var subQ2=makeQuery(id+"F2.imprint","INTERSECT",VERTEX,{"derivedFrom":[subQ1,subQ0]});Q9=makeQuery(id+"F2.imprint","IMPRINT",FACE,{"disambiguationData":[TD([[makeQuery(id+"F2.imprint","IMPRINT",EDGE,{"disambiguationData":[TD([[subQ2,1.0]])],"derivedFrom":subQ1}),1.0]])]});}
            var Q10;
            {var subQ1=sQuery(id+"F2.wireOp",EDGE,"E99.MirrorCS");var subQ3=sQuery(id+"F2.wireOp",EDGE,"E116.MirrorC");var subQ4=makeQuery(id+"F2.imprint","INTERSECT",VERTEX,{"derivedFrom":[subQ1,subQ3]});Q10=makeQuery(id+"F2.imprint","IMPRINT",FACE,{"disambiguationData":[TD([[makeQuery(id+"F2.imprint","IMPRINT",EDGE,{"disambiguationData":[TD([[subQ4,-1.0]])],"derivedFrom":subQ3}),-1.0]])]});}
            var Q11;
            {var subQ1=sQuery(id+"F2.wireOp",EDGE,"E103.MirrorCS");var subQ3=sQuery(id+"F2.wireOp",EDGE,"E114.MirrorC");var subQ4=makeQuery(id+"F2.imprint","INTERSECT",VERTEX,{"derivedFrom":[subQ1,subQ3]});Q11=makeQuery(id+"F2.imprint","IMPRINT",FACE,{"disambiguationData":[TD([[makeQuery(id+"F2.imprint","IMPRINT",EDGE,{"disambiguationData":[TD([[subQ4,1.0]])],"derivedFrom":subQ3}),1.0]])]});}
            var Q12;
            {var subQ1=sQuery(id+"F2.wireOp",EDGE,"E77");var subQ6=sQuery(id+"F2.wireOp",EDGE,"E79");var subQ9=makeQuery(id+"F2.imprint","INTERSECT",VERTEX,{"derivedFrom":[subQ1,subQ6]});Q12=makeQuery(id+"F2.imprint","IMPRINT",FACE,{"disambiguationData":[TD([[makeQuery(id+"F2.imprint","IMPRINT",EDGE,{"disambiguationData":[TD([[subQ9,-1.0]])],"derivedFrom":subQ1}),1.0]])]});}
            var Q13;
            {var subQ1=sQuery(id+"F2.wireOp",EDGE,"E77");var subQ6=sQuery(id+"F2.wireOp",EDGE,"E79");var subQ9=makeQuery(id+"F2.imprint","INTERSECT",VERTEX,{"derivedFrom":[subQ1,subQ6]});Q13=makeQuery(id+"F2.imprint","IMPRINT",FACE,{"disambiguationData":[TD([[makeQuery(id+"F2.imprint","IMPRINT",EDGE,{"disambiguationData":[TD([[subQ9,-1.0]])],"derivedFrom":subQ1}),-1.0]])]});}
            var Q14;
            {var subQ0=sQuery(id+"F2.wireOp",EDGE,"E96.MirrorCS");var subQ1=sQuery(id+"F2.wireOp",EDGE,"E90.MirrorC");var subQ2=makeQuery(id+"F2.imprint","INTERSECT",VERTEX,{"derivedFrom":[subQ1,subQ0]});Q14=makeQuery(id+"F2.imprint","IMPRINT",FACE,{"disambiguationData":[TD([[makeQuery(id+"F2.imprint","IMPRINT",EDGE,{"disambiguationData":[TD([[subQ2,1.0]])],"derivedFrom":subQ1}),1.0]])]});}
            var Q15;
            {var subQ0=sQuery(id+"F2.wireOp",EDGE,"E96.MirrorCS");var subQ1=sQuery(id+"F2.wireOp",EDGE,"E90.MirrorC");var subQ2=makeQuery(id+"F2.imprint","INTERSECT",VERTEX,{"derivedFrom":[subQ1,subQ0]});Q15=makeQuery(id+"F2.imprint","IMPRINT",FACE,{"disambiguationData":[TD([[makeQuery(id+"F2.imprint","IMPRINT",EDGE,{"disambiguationData":[TD([[subQ2,-1.0]])],"derivedFrom":subQ1}),1.0]])]});}
            var Q16;
            {var subQ0=sQuery(id+"F2.wireOp",EDGE,"E113.MirrorC");var subQ5=sQuery(id+"F2.wireOp",EDGE,"E112.MirrorCS");var subQ6=makeQuery(id+"F2.imprint","INTERSECT",VERTEX,{"derivedFrom":[subQ5,subQ0]});Q16=makeQuery(id+"F2.imprint","IMPRINT",FACE,{"disambiguationData":[TD([[makeQuery(id+"F2.imprint","IMPRINT",EDGE,{"disambiguationData":[TD([[subQ6,-1.0]])],"derivedFrom":subQ5}),-1.0]])]});}
            var Q17;
            {var subQ3=sQuery(id+"F2.wireOp",EDGE,"E108.MirrorCS");var subQ5=sQuery(id+"F2.wireOp",EDGE,"E115.MirrorC");var subQ6=makeQuery(id+"F2.imprint","INTERSECT",VERTEX,{"derivedFrom":[subQ3,subQ5]});Q17=makeQuery(id+"F2.imprint","IMPRINT",FACE,{"disambiguationData":[TD([[makeQuery(id+"F2.imprint","IMPRINT",EDGE,{"disambiguationData":[TD([[subQ6,-1.0]])],"derivedFrom":subQ3}),-1.0]])]});}
            var Q18;
            {var subQ3=sQuery(id+"F2.wireOp",EDGE,"E108.MirrorCS");var subQ5=sQuery(id+"F2.wireOp",EDGE,"E115.MirrorC");var subQ6=makeQuery(id+"F2.imprint","INTERSECT",VERTEX,{"derivedFrom":[subQ3,subQ5]});Q18=makeQuery(id+"F2.imprint","IMPRINT",FACE,{"disambiguationData":[TD([[makeQuery(id+"F2.imprint","IMPRINT",EDGE,{"disambiguationData":[TD([[subQ6,-1.0]])],"derivedFrom":subQ3}),1.0]])]});}
            var Q19;
            {var subQ0=sQuery(id+"F2.wireOp",EDGE,"E113.MirrorC");var subQ1=sQuery(id+"F2.wireOp",EDGE,"E112.MirrorCS");var subQ2=makeQuery(id+"F2.imprint","INTERSECT",VERTEX,{"derivedFrom":[subQ1,subQ0]});Q19=makeQuery(id+"F2.imprint","IMPRINT",FACE,{"disambiguationData":[TD([[makeQuery(id+"F2.imprint","IMPRINT",EDGE,{"disambiguationData":[TD([[subQ2,-1.0]])],"derivedFrom":subQ1}),1.0]])]});}
            var Q20;
            {var subQ0=sQuery(id+"F2.wireOp",EDGE,"E79");var subQ1=sQuery(id+"F2.wireOp",EDGE,"E77");var subQ2=makeQuery(id+"F2.imprint","INTERSECT",VERTEX,{"derivedFrom":[subQ1,subQ0]});Q20=makeQuery(id+"F2.imprint","IMPRINT",FACE,{"disambiguationData":[TD([[makeQuery(id+"F2.imprint","IMPRINT",EDGE,{"disambiguationData":[TD([[subQ2,1.0]])],"derivedFrom":subQ1}),1.0]])]});}
            var Q21;
            {var subQ0=sQuery(id+"F2.wireOp",EDGE,"E79");var subQ1=sQuery(id+"F2.wireOp",EDGE,"E77");var subQ2=makeQuery(id+"F2.imprint","INTERSECT",VERTEX,{"derivedFrom":[subQ1,subQ0]});Q21=makeQuery(id+"F2.imprint","IMPRINT",FACE,{"disambiguationData":[TD([[makeQuery(id+"F2.imprint","IMPRINT",EDGE,{"disambiguationData":[TD([[subQ2,1.0]])],"derivedFrom":subQ1}),-1.0]])]});}
            var Q22;
            {var subQ0=sQuery(id+"F2.wireOp",EDGE,"E97.MirrorC");var subQ1=sQuery(id+"F2.wireOp",EDGE,"E93.MirrorCS");var subQ2=makeQuery(id+"F2.imprint","INTERSECT",VERTEX,{"derivedFrom":[subQ1,subQ0]});Q22=makeQuery(id+"F2.imprint","IMPRINT",FACE,{"disambiguationData":[TD([[makeQuery(id+"F2.imprint","IMPRINT",EDGE,{"disambiguationData":[TD([[subQ2,1.0]])],"derivedFrom":subQ1}),1.0]])]});}
            var Q23;
            {var subQ0=sQuery(id+"F2.wireOp",EDGE,"E97.MirrorC");var subQ1=sQuery(id+"F2.wireOp",EDGE,"E94.MirrorCS");var subQ2=makeQuery(id+"F2.imprint","INTERSECT",VERTEX,{"derivedFrom":[subQ1,subQ0]});Q23=makeQuery(id+"F2.imprint","IMPRINT",FACE,{"disambiguationData":[TD([[makeQuery(id+"F2.imprint","IMPRINT",EDGE,{"disambiguationData":[TD([[subQ2,-1.0]])],"derivedFrom":subQ1}),1.0]])]});}
            var Q24;
            {var subQ0=sQuery(id+"F2.wireOp",EDGE,"E115.MirrorC");var subQ1=sQuery(id+"F2.wireOp",EDGE,"E108.MirrorCS");var subQ2=makeQuery(id+"F2.imprint","INTERSECT",VERTEX,{"derivedFrom":[subQ1,subQ0]});Q24=makeQuery(id+"F2.imprint","IMPRINT",FACE,{"disambiguationData":[TD([[makeQuery(id+"F2.imprint","IMPRINT",EDGE,{"disambiguationData":[TD([[subQ2,1.0]])],"derivedFrom":subQ1}),-1.0]])]});}
            var Q25;
            {var subQ0=sQuery(id+"F2.wireOp",EDGE,"E115.MirrorC");var subQ1=sQuery(id+"F2.wireOp",EDGE,"E108.MirrorCS");var subQ2=makeQuery(id+"F2.imprint","INTERSECT",VERTEX,{"derivedFrom":[subQ1,subQ0]});Q25=makeQuery(id+"F2.imprint","IMPRINT",FACE,{"disambiguationData":[TD([[makeQuery(id+"F2.imprint","IMPRINT",EDGE,{"disambiguationData":[TD([[subQ2,1.0]])],"derivedFrom":subQ1}),1.0]])]});}
            var Q26;
            {var subQ0=sQuery(id+"F2.wireOp",EDGE,"E113.MirrorC");var subQ1=sQuery(id+"F2.wireOp",EDGE,"E110.MirrorCS");var subQ2=makeQuery(id+"F2.imprint","INTERSECT",VERTEX,{"derivedFrom":[subQ1,subQ0]});Q26=makeQuery(id+"F2.imprint","IMPRINT",FACE,{"disambiguationData":[TD([[makeQuery(id+"F2.imprint","IMPRINT",EDGE,{"disambiguationData":[TD([[subQ2,-1.0]])],"derivedFrom":subQ1}),-1.0]])]});}
            var Q27;
            {var subQ0=sQuery(id+"F2.wireOp",EDGE,"E113.MirrorC");var subQ1=sQuery(id+"F2.wireOp",EDGE,"E112.MirrorCS");var subQ2=makeQuery(id+"F2.imprint","INTERSECT",VERTEX,{"derivedFrom":[subQ1,subQ0]});Q27=makeQuery(id+"F2.imprint","IMPRINT",FACE,{"disambiguationData":[TD([[makeQuery(id+"F2.imprint","IMPRINT",EDGE,{"disambiguationData":[TD([[subQ2,1.0]])],"derivedFrom":subQ1}),1.0]])]});}
            var Q28;
            {var subQ4=makeQuery(id+"F1.opExtrude","CAP_EDGE",EDGE,{"disambiguationData":[OSD([sQuery(id+"F0.wireOp",EDGE,"E9.MirrorC")])],"isStart":false});var subQ7=sQuery(id+"F2.wireOp",EDGE,"E77");var subQ8=makeQuery(id+"F2.imprint","INTERSECT",VERTEX,{"derivedFrom":[subQ4,subQ7]});Q28=makeQuery(id+"F2.imprint","IMPRINT",FACE,{"disambiguationData":[TD([[makeQuery(id+"F2.imprint","IMPRINT",EDGE,{"disambiguationData":[TD([[subQ8,-1.0]])],"derivedFrom":subQ7}),1.0]])]});}
            var Q29;
            {var subQ3=sQuery(id+"F2.wireOp",EDGE,"E77");var subQ7=makeQuery(id+"F1.opExtrude","CAP_EDGE",EDGE,{"disambiguationData":[OSD([sQuery(id+"F0.wireOp",EDGE,"E9.MirrorC")])],"isStart":false});var subQ9=makeQuery(id+"F2.imprint","INTERSECT",VERTEX,{"derivedFrom":[subQ7,subQ3]});Q29=makeQuery(id+"F2.imprint","IMPRINT",FACE,{"disambiguationData":[TD([[makeQuery(id+"F2.imprint","IMPRINT",EDGE,{"disambiguationData":[TD([[subQ9,-1.0]])],"derivedFrom":subQ3}),-1.0]])]});}
            var Q30;
            {var subQ3=sQuery(id+"F2.wireOp",EDGE,"E96.MirrorCS");var subQ5=makeQuery(id+"F1.opExtrude","CAP_EDGE",EDGE,{"disambiguationData":[OSD([sQuery(id+"F0.wireOp",EDGE,"E7.MirrorC")])],"isStart":false});var subQ6=makeQuery(id+"F2.imprint","INTERSECT",VERTEX,{"derivedFrom":[subQ5,subQ3]});Q30=makeQuery(id+"F2.imprint","IMPRINT",FACE,{"disambiguationData":[TD([[makeQuery(id+"F2.imprint","IMPRINT",EDGE,{"disambiguationData":[TD([[subQ6,-1.0]])],"derivedFrom":subQ3}),1.0]])]});}
            var Q31;
            {var subQ0=sQuery(id+"F2.wireOp",EDGE,"E96.MirrorCS");var subQ1=makeQuery(id+"F1.opExtrude","CAP_EDGE",EDGE,{"disambiguationData":[OSD([sQuery(id+"F0.wireOp",EDGE,"E7.MirrorC")])],"isStart":false});var subQ2=makeQuery(id+"F2.imprint","INTERSECT",VERTEX,{"derivedFrom":[subQ1,subQ0]});Q31=makeQuery(id+"F2.imprint","IMPRINT",FACE,{"disambiguationData":[TD([[makeQuery(id+"F2.imprint","IMPRINT",EDGE,{"disambiguationData":[TD([[subQ2,-1.0]])],"derivedFrom":subQ0}),-1.0]])]});}
            var Q32;
            {var subQ0=sQuery(id+"F2.wireOp",EDGE,"E112.MirrorCS");var subQ1=makeQuery(id+"F1.opExtrude","CAP_EDGE",EDGE,{"disambiguationData":[OSD([sQuery(id+"F0.wireOp",EDGE,"E3")])],"isStart":false});var subQ2=makeQuery(id+"F2.imprint","INTERSECT",VERTEX,{"derivedFrom":[subQ1,subQ0]});Q32=makeQuery(id+"F2.imprint","IMPRINT",FACE,{"disambiguationData":[TD([[makeQuery(id+"F2.imprint","IMPRINT",EDGE,{"disambiguationData":[TD([[subQ2,-1.0]])],"derivedFrom":subQ0}),-1.0]])]});}
            var Q33;
            {var subQ3=sQuery(id+"F2.wireOp",EDGE,"E108.MirrorCS");var subQ5=makeQuery(id+"F1.opExtrude","CAP_EDGE",EDGE,{"disambiguationData":[OSD([sQuery(id+"F0.wireOp",EDGE,"E5.MirrorC")])],"isStart":false});var subQ6=makeQuery(id+"F2.imprint","INTERSECT",VERTEX,{"derivedFrom":[subQ5,subQ3]});Q33=makeQuery(id+"F2.imprint","IMPRINT",FACE,{"disambiguationData":[TD([[makeQuery(id+"F2.imprint","IMPRINT",EDGE,{"disambiguationData":[TD([[subQ6,-1.0]])],"derivedFrom":subQ3}),-1.0]])]});}
            var Q34;
            {var subQ3=sQuery(id+"F2.wireOp",EDGE,"E108.MirrorCS");var subQ5=makeQuery(id+"F1.opExtrude","CAP_EDGE",EDGE,{"disambiguationData":[OSD([sQuery(id+"F0.wireOp",EDGE,"E5.MirrorC")])],"isStart":false});var subQ6=makeQuery(id+"F2.imprint","INTERSECT",VERTEX,{"derivedFrom":[subQ5,subQ3]});Q34=makeQuery(id+"F2.imprint","IMPRINT",FACE,{"disambiguationData":[TD([[makeQuery(id+"F2.imprint","IMPRINT",EDGE,{"disambiguationData":[TD([[subQ6,-1.0]])],"derivedFrom":subQ3}),1.0]])]});}
            var Q35;
            {var subQ3=sQuery(id+"F2.wireOp",EDGE,"E112.MirrorCS");var subQ7=makeQuery(id+"F1.opExtrude","CAP_EDGE",EDGE,{"disambiguationData":[OSD([sQuery(id+"F0.wireOp",EDGE,"E3")])],"isStart":false});var subQ8=makeQuery(id+"F2.imprint","INTERSECT",VERTEX,{"derivedFrom":[subQ7,subQ3]});Q35=makeQuery(id+"F2.imprint","IMPRINT",FACE,{"disambiguationData":[TD([[makeQuery(id+"F2.imprint","IMPRINT",EDGE,{"disambiguationData":[TD([[subQ8,-1.0]])],"derivedFrom":subQ3}),1.0]])]});}
            extrude(context, id + "F3", {"entities" : qUnion([Q0, Q1, Q2, Q3, Q4, Q5, Q6, Q7, Q8, Q9, Q10, Q11, Q12, Q13, Q14, Q15, Q16, Q17, Q18, Q19, Q20, Q21, Q22, Q23, Q24, Q25, Q26, Q27, Q28, Q29, Q30, Q31, Q32, Q33, Q34, Q35]), "operationType" : NewBodyOperationType.ADD, "oppositeDirection" : true, "depth" : 3.17 * mm});
        }
        {
            var Q0;
            {var subQ0=sQuery(id+"F0.wireOp",EDGE,"E5.MirrorC");var subQ1=sQuery(id+"F0.wireOp",EDGE,"E3");var subQ2=sQuery(id+"F0.wireOp",EDGE,"E7.MirrorC");var subQ3=sQuery(id+"F0.wireOp",EDGE,"E9.MirrorC");Q0=makeQuery(id+"F3.boolean.opBoolean","MERGE",FACE,{"derivedFrom":[makeQuery(id+"F1.opExtrude","CAP_FACE",FACE,{"disambiguationData":[OSD([sQuery(id+"F0.wireOp",EDGE,"E1.bottom"),sQuery(id+"F0.wireOp",EDGE,"E1.left"),sQuery(id+"F0.wireOp",EDGE,"E1.right"),sQuery(id+"F0.wireOp",EDGE,"E2"),subQ1,sQuery(id+"F0.wireOp",EDGE,"E4.MirrorC"),subQ0,sQuery(id+"F0.wireOp",EDGE,"E6.MirrorC"),subQ2,sQuery(id+"F0.wireOp",EDGE,"E8.MirrorC"),subQ3,sQuery(id+"F0.wireOp",EDGE,"E11"),sQuery(id+"F0.wireOp",EDGE,"E13.MirrorCS"),sQuery(id+"F0.wireOp",EDGE,"E14.MirrorCS"),sQuery(id+"F0.wireOp",EDGE,"E15.MirrorCS"),sQuery(id+"F0.wireOp",EDGE,"E16.0"),sQuery(id+"F0.wireOp",EDGE,"E16.1"),sQuery(id+"F0.wireOp",EDGE,"E16.2"),sQuery(id+"F0.wireOp",EDGE,"E16.3"),sQuery(id+"F0.wireOp",EDGE,"E17.right"),sQuery(id+"F0.wireOp",EDGE,"E18.MirrorCS"),sQuery(id+"F0.wireOp",EDGE,"E22.MirrorCS"),sQuery(id+"F0.wireOp",EDGE,"E23.MirrorCS"),sQuery(id+"F0.wireOp",EDGE,"E24.MirrorCS"),sQuery(id+"F0.wireOp",EDGE,"E26.top"),sQuery(id+"F0.wireOp",EDGE,"E27.MirrorCS"),sQuery(id+"F0.wireOp",EDGE,"E31.MirrorCS"),sQuery(id+"F0.wireOp",EDGE,"E32.MirrorCS"),sQuery(id+"F0.wireOp",EDGE,"E36"),sQuery(id+"F0.wireOp",EDGE,"E38"),sQuery(id+"F0.wireOp",EDGE,"E39.MirrorCS"),sQuery(id+"F0.wireOp",EDGE,"E41.MirrorCS"),sQuery(id+"F0.wireOp",EDGE,"E43.MirrorCS"),sQuery(id+"F0.wireOp",EDGE,"E45.MirrorCS"),sQuery(id+"F0.wireOp",EDGE,"E47.MirrorCS"),sQuery(id+"F0.wireOp",EDGE,"E49.MirrorCS")])],"isStart":false}),makeQuery(id+"F3.opExtrude","CAP_FACE",FACE,{"disambiguationData":[OSD([subQ3,sQuery(id+"F2.wireOp",EDGE,"E79"),sQuery(id+"F2.wireOp",EDGE,"E80"),sQuery(id+"F2.wireOp",EDGE,"E83"),sQuery(id+"F2.wireOp",EDGE,"E84"),sQuery(id+"F2.wireOp",EDGE,"E85"),sQuery(id+"F2.wireOp",EDGE,"E86")])],"isStart":true}),makeQuery(id+"F3.opExtrude","CAP_FACE",FACE,{"disambiguationData":[OSD([subQ2,sQuery(id+"F2.wireOp",EDGE,"E87.MirrorCS"),sQuery(id+"F2.wireOp",EDGE,"E88.MirrorCS"),sQuery(id+"F2.wireOp",EDGE,"E90.MirrorC"),sQuery(id+"F2.wireOp",EDGE,"E93.MirrorCS"),sQuery(id+"F2.wireOp",EDGE,"E94.MirrorCS"),sQuery(id+"F2.wireOp",EDGE,"E97.MirrorC")])],"isStart":true}),makeQuery(id+"F3.opExtrude","CAP_FACE",FACE,{"disambiguationData":[OSD([subQ1,sQuery(id+"F2.wireOp",EDGE,"E98.MirrorCS"),sQuery(id+"F2.wireOp",EDGE,"E102.MirrorCS"),sQuery(id+"F2.wireOp",EDGE,"E110.MirrorCS"),sQuery(id+"F2.wireOp",EDGE,"E113.MirrorC"),sQuery(id+"F2.wireOp",EDGE,"E116.MirrorC"),sQuery(id+"F2.wireOp",EDGE,"E117.MirrorCS")])],"isStart":true}),makeQuery(id+"F3.opExtrude","CAP_FACE",FACE,{"disambiguationData":[OSD([subQ0,sQuery(id+"F2.wireOp",EDGE,"E100.MirrorCS"),sQuery(id+"F2.wireOp",EDGE,"E101.MirrorCS"),sQuery(id+"F2.wireOp",EDGE,"E114.MirrorC"),sQuery(id+"F2.wireOp",EDGE,"E115.MirrorC"),sQuery(id+"F2.wireOp",EDGE,"E118.MirrorCS"),sQuery(id+"F2.wireOp",EDGE,"E119.MirrorCS")])],"isStart":true})]});}
            var sketch = newSketch(context, id + "F4", { "sketchPlane" : qUnion([Q0])});
            skLineSegment(sketch, "E120", {"start": v(-32.7, -32.33) * mm, "end": v(-30.46, -30.08) * mm});
            skLineSegment(sketch, "E121", {"start": v(-32.7, -32.33) * mm, "end": v(-32.7, -29.15) * mm});
            skLineSegment(sketch, "E122", {"start": v(-19.05, -19.05) * mm, "end": v(-20.22, -20.22) * mm});
            skLineSegment(sketch, "E123", {"start": v(-19.05, -19.05) * mm, "end": v(-19.05, -17.4) * mm});
            skLineSegment(sketch, "E124", {"start": v(-30.46, -30.08) * mm, "end": v(-20.22, -20.22) * mm});
            skPoint(sketch, "E125", {"position": v(-29.32, -28.98) * mm});
            skPoint(sketch, "E126", {"position": v(-21.36, -21.32) * mm});
            skCircle(sketch, "E127", {"center": v(-28.18, -27.88) * mm, "radius": 1.59 * mm});
            skPoint(sketch, "E127.second.point", {"position": v(-27.03, -26.78) * mm});
            skPoint(sketch, "E127.third.point", {"position": v(-29.07, -26.57) * mm});
            skCircle(sketch, "E128", {"center": v(-22.5, -22.42) * mm, "radius": 1.59 * mm});
            skPoint(sketch, "E128.second.point", {"position": v(-23.65, -23.52) * mm});
            skPoint(sketch, "E128.third.point", {"position": v(-21.36, -23.52) * mm});
            skLineSegment(sketch, "E129", {"start": v(-28.18, -27.88) * mm, "end": v(-27.08, -29.03) * mm});
            skLineSegment(sketch, "E130", {"start": v(-28.18, -27.88) * mm, "end": v(-29.28, -26.74) * mm});
            skLineSegment(sketch, "E131", {"start": v(-22.5, -22.42) * mm, "end": v(-23.6, -21.28) * mm});
            skLineSegment(sketch, "E132", {"start": v(-22.5, -22.42) * mm, "end": v(-21.4, -23.56) * mm});
            skArc(sketch, "E133", {"start": v(-21.4, -23.56) * mm, "mid": v(-24.35, -26.18) * mm, "end": v(-27.08, -29.03) * mm});
            skArc(sketch, "E134", {"start": v(-29.28, -26.74) * mm, "mid": v(-26.34, -24.12) * mm, "end": v(-23.6, -21.28) * mm});
            skLineSegment(sketch, "E135.MirrorCS", {"start": v(-22.5, 22.42) * mm, "end": v(-23.6, 21.28) * mm});
            skLineSegment(sketch, "E136.MirrorCS", {"start": v(-22.5, 22.42) * mm, "end": v(-21.4, 23.56) * mm});
            skLineSegment(sketch, "E137.MirrorCS", {"start": v(-28.18, 27.88) * mm, "end": v(-29.28, 26.74) * mm});
            skLineSegment(sketch, "E138.MirrorCS", {"start": v(-28.18, 27.88) * mm, "end": v(-27.08, 29.03) * mm});
            skLineSegment(sketch, "E139.MirrorCS", {"start": v(-19.05, 19.05) * mm, "end": v(-20.22, 20.22) * mm});
            skLineSegment(sketch, "E140.MirrorCS", {"start": v(-32.7, 32.33) * mm, "end": v(-30.46, 30.08) * mm});
            skLineSegment(sketch, "E141.MirrorCS", {"start": v(-32.7, 32.33) * mm, "end": v(-32.7, 29.15) * mm});
            skCircle(sketch, "E142.MirrorC", {"center": v(-22.5, 22.42) * mm, "radius": 1.59 * mm});
            skCircle(sketch, "E143.MirrorC", {"center": v(-28.18, 27.88) * mm, "radius": 1.59 * mm});
            skLineSegment(sketch, "E144.MirrorCS", {"start": v(-30.46, 30.08) * mm, "end": v(-20.22, 20.22) * mm});
            skLineSegment(sketch, "E145.MirrorCS", {"start": v(-19.05, 19.05) * mm, "end": v(-19.05, 17.4) * mm});
            skPoint(sketch, "E146.MirrorP", {"position": v(-29.32, 28.98) * mm});
            skPoint(sketch, "E147.MirrorP", {"position": v(-27.03, 26.78) * mm});
            skPoint(sketch, "E148.MirrorP", {"position": v(-29.07, 26.57) * mm});
            skPoint(sketch, "E149.MirrorP", {"position": v(-23.65, 23.52) * mm});
            skPoint(sketch, "E150.MirrorP", {"position": v(-21.36, 23.52) * mm});
            skPoint(sketch, "E151.MirrorP", {"position": v(-21.36, 21.32) * mm});
            skArc(sketch, "E152.MirrorCS", {"start": v(-29.28, 26.74) * mm, "mid": v(-26.34, 24.12) * mm, "end": v(-23.6, 21.28) * mm});
            skArc(sketch, "E153.MirrorCS", {"start": v(-21.4, 23.56) * mm, "mid": v(-24.35, 26.18) * mm, "end": v(-27.08, 29.03) * mm});
            skLineSegment(sketch, "E154.MirrorCS", {"start": v(22.5, -22.42) * mm, "end": v(21.4, -23.56) * mm});
            skLineSegment(sketch, "E155.MirrorCS", {"start": v(22.5, -22.42) * mm, "end": v(23.6, -21.28) * mm});
            skLineSegment(sketch, "E156.MirrorCS", {"start": v(28.18, -27.88) * mm, "end": v(29.28, -26.74) * mm});
            skLineSegment(sketch, "E157.MirrorCS", {"start": v(28.18, -27.88) * mm, "end": v(27.08, -29.03) * mm});
            skLineSegment(sketch, "E158.MirrorCS", {"start": v(19.05, -19.05) * mm, "end": v(20.22, -20.22) * mm});
            skLineSegment(sketch, "E159.MirrorCS", {"start": v(28.18, 27.88) * mm, "end": v(29.28, 26.74) * mm});
            skLineSegment(sketch, "E160.MirrorCS", {"start": v(22.5, 22.42) * mm, "end": v(21.4, 23.56) * mm});
            skLineSegment(sketch, "E161.MirrorCS", {"start": v(28.18, 27.88) * mm, "end": v(27.08, 29.03) * mm});
            skLineSegment(sketch, "E162.MirrorCS", {"start": v(22.5, 22.42) * mm, "end": v(23.6, 21.28) * mm});
            skCircle(sketch, "E163.MirrorC", {"center": v(28.18, 27.88) * mm, "radius": 1.59 * mm});
            skCircle(sketch, "E164.MirrorC", {"center": v(22.5, -22.42) * mm, "radius": 1.59 * mm});
            skLineSegment(sketch, "E165.MirrorCS", {"start": v(32.7, -32.33) * mm, "end": v(30.46, -30.08) * mm});
            skLineSegment(sketch, "E166.MirrorCS", {"start": v(19.05, 19.05) * mm, "end": v(19.05, 17.4) * mm});
            skLineSegment(sketch, "E167.MirrorCS", {"start": v(19.05, 19.05) * mm, "end": v(20.22, 20.22) * mm});
            skLineSegment(sketch, "E168.MirrorCS", {"start": v(32.7, 32.33) * mm, "end": v(30.46, 30.08) * mm});
            skCircle(sketch, "E169.MirrorC", {"center": v(28.18, -27.88) * mm, "radius": 1.59 * mm});
            skLineSegment(sketch, "E170.MirrorCS", {"start": v(30.46, -30.08) * mm, "end": v(20.22, -20.22) * mm});
            skLineSegment(sketch, "E171.MirrorCS", {"start": v(19.05, -19.05) * mm, "end": v(19.05, -17.4) * mm});
            skLineSegment(sketch, "E172.MirrorCS", {"start": v(32.7, -32.33) * mm, "end": v(32.7, -29.15) * mm});
            skCircle(sketch, "E173.MirrorC", {"center": v(22.5, 22.42) * mm, "radius": 1.59 * mm});
            skLineSegment(sketch, "E174.MirrorCS", {"start": v(30.46, 30.08) * mm, "end": v(20.22, 20.22) * mm});
            skLineSegment(sketch, "E175.MirrorCS", {"start": v(32.7, 32.33) * mm, "end": v(32.7, 29.15) * mm});
            skPoint(sketch, "E176.MirrorP", {"position": v(27.03, -26.78) * mm});
            skPoint(sketch, "E177.MirrorP", {"position": v(29.32, -28.98) * mm});
            skPoint(sketch, "E178.MirrorP", {"position": v(21.36, 23.52) * mm});
            skArc(sketch, "E179.MirrorCS", {"start": v(29.28, -26.74) * mm, "mid": v(26.34, -24.12) * mm, "end": v(23.6, -21.28) * mm});
            skArc(sketch, "E180.MirrorCS", {"start": v(21.4, -23.56) * mm, "mid": v(24.35, -26.18) * mm, "end": v(27.08, -29.03) * mm});
            skPoint(sketch, "E181.MirrorP", {"position": v(23.65, 23.52) * mm});
            skPoint(sketch, "E182.MirrorP", {"position": v(21.36, -21.32) * mm});
            skPoint(sketch, "E183.MirrorP", {"position": v(21.36, 21.32) * mm});
            skArc(sketch, "E184.MirrorCS", {"start": v(29.28, 26.74) * mm, "mid": v(26.34, 24.12) * mm, "end": v(23.6, 21.28) * mm});
            skPoint(sketch, "E185.MirrorP", {"position": v(29.07, 26.57) * mm});
            skPoint(sketch, "E186.MirrorP", {"position": v(29.07, -26.57) * mm});
            skPoint(sketch, "E187.MirrorP", {"position": v(29.32, 28.98) * mm});
            skPoint(sketch, "E188.MirrorP", {"position": v(23.65, -23.52) * mm});
            skArc(sketch, "E189.MirrorCS", {"start": v(21.4, 23.56) * mm, "mid": v(24.35, 26.18) * mm, "end": v(27.08, 29.03) * mm});
            skPoint(sketch, "E190.MirrorP", {"position": v(27.03, 26.78) * mm});
            skPoint(sketch, "E191.MirrorP", {"position": v(21.36, -23.52) * mm});
            skSolve(sketch);
        }
        {
            var Q0;
            Q0 = qSketchRegion(id + "F4", true);
            extrude(context, id + "F5", {"entities" : qUnion([Q0]), "operationType" : NewBodyOperationType.REMOVE, "oppositeDirection" : true, "depth" : 25.4 * mm});
        }
        {
            var Q0;
            {var subQ0=sQuery(id+"F2.wireOp",EDGE,"E96.MirrorCS");var subQ1=sQuery(id+"F2.wireOp",EDGE,"E90.MirrorC");var subQ2=makeQuery(id+"F2.imprint","INTERSECT",VERTEX,{"derivedFrom":[subQ1,subQ0]});Q0=makeQuery(id+"F2.imprint","IMPRINT",FACE,{"disambiguationData":[TD([[makeQuery(id+"F2.imprint","IMPRINT",EDGE,{"disambiguationData":[TD([[subQ2,-1.0]])],"derivedFrom":subQ1}),1.0]])]});}
            var Q1;
            {var subQ0=sQuery(id+"F2.wireOp",EDGE,"E96.MirrorCS");var subQ1=sQuery(id+"F2.wireOp",EDGE,"E90.MirrorC");var subQ2=makeQuery(id+"F2.imprint","INTERSECT",VERTEX,{"derivedFrom":[subQ1,subQ0]});Q1=makeQuery(id+"F2.imprint","IMPRINT",FACE,{"disambiguationData":[TD([[makeQuery(id+"F2.imprint","IMPRINT",EDGE,{"disambiguationData":[TD([[subQ2,1.0]])],"derivedFrom":subQ1}),1.0]])]});}
            var Q2;
            {var subQ0=sQuery(id+"F2.wireOp",EDGE,"E92.MirrorCS");var subQ1=sQuery(id+"F2.wireOp",EDGE,"E90.MirrorC");var subQ2=makeQuery(id+"F2.imprint","INTERSECT",VERTEX,{"derivedFrom":[subQ1,subQ0]});Q2=makeQuery(id+"F2.imprint","IMPRINT",FACE,{"disambiguationData":[TD([[makeQuery(id+"F2.imprint","IMPRINT",EDGE,{"disambiguationData":[TD([[subQ2,1.0]])],"derivedFrom":subQ1}),1.0]])]});}
            var Q3;
            {var subQ1=sQuery(id+"F2.wireOp",EDGE,"E103.MirrorCS");var subQ3=sQuery(id+"F2.wireOp",EDGE,"E114.MirrorC");var subQ4=makeQuery(id+"F2.imprint","INTERSECT",VERTEX,{"derivedFrom":[subQ1,subQ3]});Q3=makeQuery(id+"F2.imprint","IMPRINT",FACE,{"disambiguationData":[TD([[makeQuery(id+"F2.imprint","IMPRINT",EDGE,{"disambiguationData":[TD([[subQ4,1.0]])],"derivedFrom":subQ3}),1.0]])]});}
            var Q4;
            {var subQ3=sQuery(id+"F2.wireOp",EDGE,"E108.MirrorCS");var subQ5=sQuery(id+"F2.wireOp",EDGE,"E115.MirrorC");var subQ6=makeQuery(id+"F2.imprint","INTERSECT",VERTEX,{"derivedFrom":[subQ3,subQ5]});Q4=makeQuery(id+"F2.imprint","IMPRINT",FACE,{"disambiguationData":[TD([[makeQuery(id+"F2.imprint","IMPRINT",EDGE,{"disambiguationData":[TD([[subQ6,-1.0]])],"derivedFrom":subQ3}),1.0]])]});}
            var Q5;
            {var subQ3=sQuery(id+"F2.wireOp",EDGE,"E108.MirrorCS");var subQ5=sQuery(id+"F2.wireOp",EDGE,"E115.MirrorC");var subQ6=makeQuery(id+"F2.imprint","INTERSECT",VERTEX,{"derivedFrom":[subQ3,subQ5]});Q5=makeQuery(id+"F2.imprint","IMPRINT",FACE,{"disambiguationData":[TD([[makeQuery(id+"F2.imprint","IMPRINT",EDGE,{"disambiguationData":[TD([[subQ6,-1.0]])],"derivedFrom":subQ3}),-1.0]])]});}
            var Q6;
            {var subQ0=sQuery(id+"F2.wireOp",EDGE,"E113.MirrorC");var subQ5=sQuery(id+"F2.wireOp",EDGE,"E112.MirrorCS");var subQ6=makeQuery(id+"F2.imprint","INTERSECT",VERTEX,{"derivedFrom":[subQ5,subQ0]});Q6=makeQuery(id+"F2.imprint","IMPRINT",FACE,{"disambiguationData":[TD([[makeQuery(id+"F2.imprint","IMPRINT",EDGE,{"disambiguationData":[TD([[subQ6,-1.0]])],"derivedFrom":subQ5}),-1.0]])]});}
            var Q7;
            {var subQ1=sQuery(id+"F2.wireOp",EDGE,"E99.MirrorCS");var subQ3=sQuery(id+"F2.wireOp",EDGE,"E116.MirrorC");var subQ4=makeQuery(id+"F2.imprint","INTERSECT",VERTEX,{"derivedFrom":[subQ1,subQ3]});Q7=makeQuery(id+"F2.imprint","IMPRINT",FACE,{"disambiguationData":[TD([[makeQuery(id+"F2.imprint","IMPRINT",EDGE,{"disambiguationData":[TD([[subQ4,-1.0]])],"derivedFrom":subQ3}),-1.0]])]});}
            var Q8;
            {var subQ0=sQuery(id+"F2.wireOp",EDGE,"E113.MirrorC");var subQ1=sQuery(id+"F2.wireOp",EDGE,"E112.MirrorCS");var subQ2=makeQuery(id+"F2.imprint","INTERSECT",VERTEX,{"derivedFrom":[subQ1,subQ0]});Q8=makeQuery(id+"F2.imprint","IMPRINT",FACE,{"disambiguationData":[TD([[makeQuery(id+"F2.imprint","IMPRINT",EDGE,{"disambiguationData":[TD([[subQ2,-1.0]])],"derivedFrom":subQ1}),1.0]])]});}
            var Q9;
            {var subQ3=sQuery(id+"F2.wireOp",EDGE,"E82");var subQ5=sQuery(id+"F2.wireOp",EDGE,"E80");var subQ7=makeQuery(id+"F2.imprint","INTERSECT",VERTEX,{"derivedFrom":[subQ5,subQ3]});Q9=makeQuery(id+"F2.imprint","IMPRINT",FACE,{"disambiguationData":[TD([[makeQuery(id+"F2.imprint","IMPRINT",EDGE,{"disambiguationData":[TD([[subQ7,1.0]])],"derivedFrom":subQ5}),-1.0]])]});}
            var Q10;
            {var subQ1=sQuery(id+"F2.wireOp",EDGE,"E77");var subQ6=sQuery(id+"F2.wireOp",EDGE,"E79");var subQ9=makeQuery(id+"F2.imprint","INTERSECT",VERTEX,{"derivedFrom":[subQ1,subQ6]});Q10=makeQuery(id+"F2.imprint","IMPRINT",FACE,{"disambiguationData":[TD([[makeQuery(id+"F2.imprint","IMPRINT",EDGE,{"disambiguationData":[TD([[subQ9,-1.0]])],"derivedFrom":subQ1}),1.0]])]});}
            var Q11;
            {var subQ1=sQuery(id+"F2.wireOp",EDGE,"E77");var subQ6=sQuery(id+"F2.wireOp",EDGE,"E79");var subQ9=makeQuery(id+"F2.imprint","INTERSECT",VERTEX,{"derivedFrom":[subQ1,subQ6]});Q11=makeQuery(id+"F2.imprint","IMPRINT",FACE,{"disambiguationData":[TD([[makeQuery(id+"F2.imprint","IMPRINT",EDGE,{"disambiguationData":[TD([[subQ9,-1.0]])],"derivedFrom":subQ1}),-1.0]])]});}
            extrude(context, id + "F6", {"entities" : qUnion([Q0, Q1, Q2, Q3, Q4, Q5, Q6, Q7, Q8, Q9, Q10, Q11]), "operationType" : NewBodyOperationType.ADD, "depth" : 9.52 * mm});
        }
        {
            var Q0;
            {var subQ5=makeQuery(id+"F1.opExtrude","CAP_EDGE",EDGE,{"disambiguationData":[OSD([sQuery(id+"F0.wireOp",EDGE,"E11")])],"isStart":false});Q0=makeQuery(id+"F2.imprint","IMPRINT",FACE,{"disambiguationData":[TD([[makeQuery(id+"F2.imprint","IMPRINT",EDGE,{"derivedFrom":subQ5}),-1.0]])]});}
            var sketch = newSketch(context, id + "F7", { "sketchPlane" : qUnion([Q0])});
            skCircle(sketch, "E192", {"center": v(0, 0) * mm, "radius": 6.35 * mm});
            skSolve(sketch);
        }
        {
            var Q0;
            Q0 = qSketchRegion(id + "F7", true);
            extrude(context, id + "F8", {"entities" : qUnion([Q0]), "operationType" : NewBodyOperationType.REMOVE, "oppositeDirection" : true, "depth" : 25.4 * mm});
        }
    });
